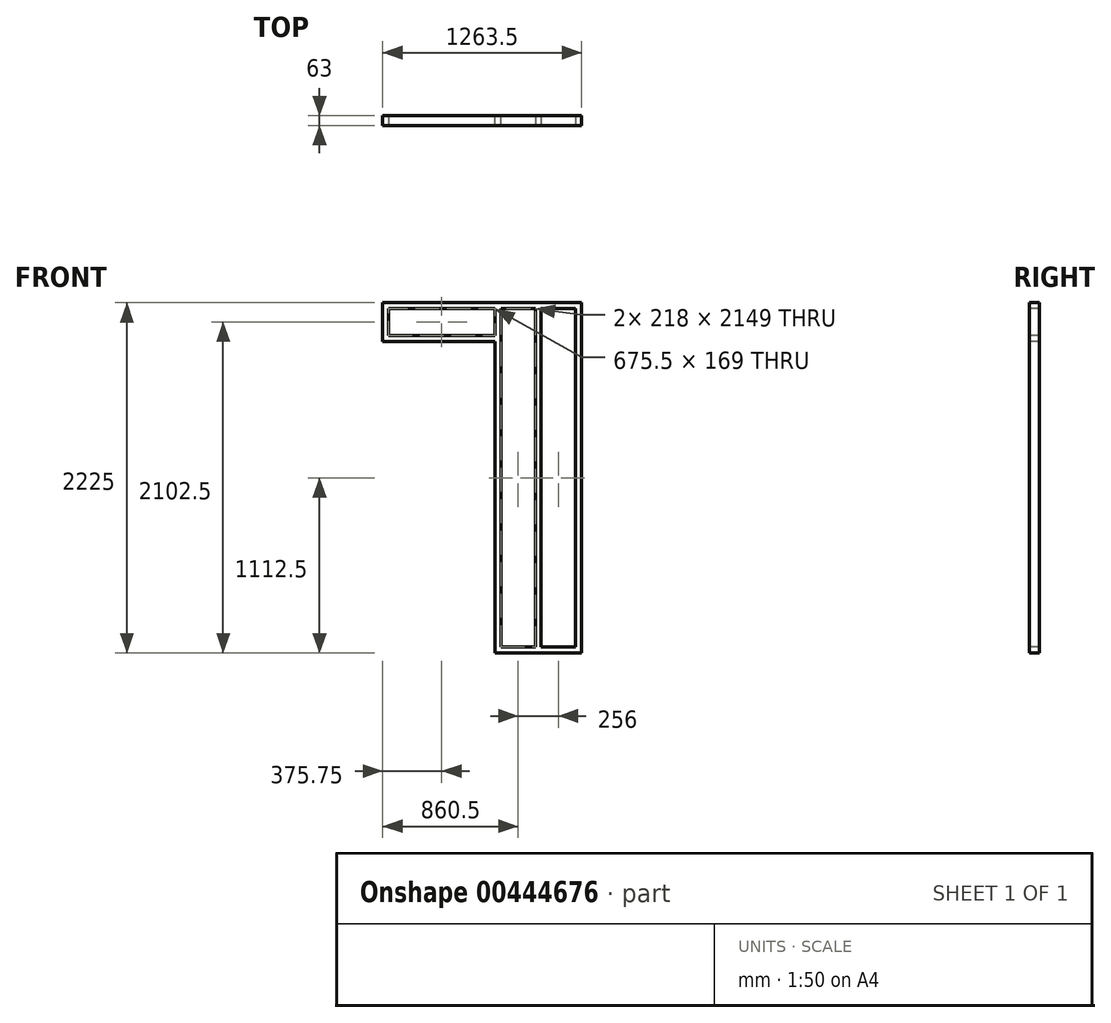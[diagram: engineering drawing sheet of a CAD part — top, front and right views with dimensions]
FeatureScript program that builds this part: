
annotation { "Feature Type Name" : "Feature", "Feature Type Description" : "" }
export const myFeature = defineFeature(function(context is Context, id is Id, definition is map)
    precondition{}
    {
        {
            var Q0;
            Q0=qCreatedBy(makeId("Top.planeOp"),FACE);
            var sketch = newSketch(context, id + "F0", { "sketchPlane" : qUnion([Q0])});
            skLineSegment(sketch, "E0.bottom", {"start": v(0, 0) * mm, "end": v(-550, 0) * mm});
            skLineSegment(sketch, "E0.top", {"start": v(0, 63) * mm, "end": v(-550, 63) * mm});
            skLineSegment(sketch, "E0.left", {"start": v(0, 0) * mm, "end": v(0, 63) * mm});
            skLineSegment(sketch, "E0.right", {"start": v(-550, 0) * mm, "end": v(-550, 63) * mm});
            skSolve(sketch);
        }
        {
            var Q0;
            Q0 = qSketchRegion(id + "F0", true);
            extrude(context, id + "F1", {"entities" : qUnion([Q0]), "depth" : 38 * mm});
        }
        {
            var Q0;
            Q0=makeQuery(id+"F1.opExtrude","CAP_FACE",FACE,{"disambiguationData":[OSD([sQuery(id+"F0.wireOp",EDGE,"E0.bottom"),sQuery(id+"F0.wireOp",EDGE,"E0.top"),sQuery(id+"F0.wireOp",EDGE,"E0.left"),sQuery(id+"F0.wireOp",EDGE,"E0.right")])],"isStart":false});
            var sketch = newSketch(context, id + "F2", { "sketchPlane" : qUnion([Q0])});
            skLineSegment(sketch, "E1.bottom", {"start": v(-550, 0) * mm, "end": v(-512, 0) * mm});
            skLineSegment(sketch, "E1.top", {"start": v(-550, 63) * mm, "end": v(-512, 63) * mm});
            skLineSegment(sketch, "E1.left", {"start": v(-550, 0) * mm, "end": v(-550, 63) * mm});
            skLineSegment(sketch, "E1.right", {"start": v(-512, 0) * mm, "end": v(-512, 63) * mm});
            skSolve(sketch);
        }
        {
            var Q0;
            Q0 = qSketchRegion(id + "F2", true);
            extrude(context, id + "F3", {"entities" : qUnion([Q0]), "operationType" : NewBodyOperationType.ADD, "depth" : 2149 * mm});
        }
        {
            var Q0;
            Q0=makeQuery(id+"F1.opExtrude","CAP_FACE",FACE,{"disambiguationData":[OSD([sQuery(id+"F0.wireOp",EDGE,"E0.bottom"),sQuery(id+"F0.wireOp",EDGE,"E0.top"),sQuery(id+"F0.wireOp",EDGE,"E0.left"),sQuery(id+"F0.wireOp",EDGE,"E0.right")])],"isStart":false});
            var sketch = newSketch(context, id + "F4", { "sketchPlane" : qUnion([Q0])});
            skLineSegment(sketch, "E2.bottom", {"start": v(0, 63) * mm, "end": v(-38, 63) * mm});
            skLineSegment(sketch, "E2.top", {"start": v(0, 0) * mm, "end": v(-38, 0) * mm});
            skLineSegment(sketch, "E2.left", {"start": v(0, 63) * mm, "end": v(0, 0) * mm});
            skLineSegment(sketch, "E2.right", {"start": v(-38, 63) * mm, "end": v(-38, 0) * mm});
            skSolve(sketch);
        }
        {
            var Q0;
            Q0 = qSketchRegion(id + "F4", true);
            extrude(context, id + "F5", {"entities" : qUnion([Q0]), "operationType" : NewBodyOperationType.ADD, "depth" : 2149 * mm});
        }
        {
            var Q0;
            Q0=makeQuery(id+"F1.opExtrude","CAP_FACE",FACE,{"disambiguationData":[OSD([sQuery(id+"F0.wireOp",EDGE,"E0.bottom"),sQuery(id+"F0.wireOp",EDGE,"E0.top"),sQuery(id+"F0.wireOp",EDGE,"E0.left"),sQuery(id+"F0.wireOp",EDGE,"E0.right")])],"isStart":false});
            var sketch = newSketch(context, id + "F6", { "sketchPlane" : qUnion([Q0])});
            skLineSegment(sketch, "E3.bottom", {"start": v(-294, 63) * mm, "end": v(-256, 63) * mm});
            skLineSegment(sketch, "E3.top", {"start": v(-294, 0) * mm, "end": v(-256, 0) * mm});
            skLineSegment(sketch, "E3.left", {"start": v(-294, 63) * mm, "end": v(-294, 0) * mm});
            skLineSegment(sketch, "E3.right", {"start": v(-256, 63) * mm, "end": v(-256, 0) * mm});
            skSolve(sketch);
        }
        {
            var Q0;
            Q0 = qSketchRegion(id + "F6", true);
            extrude(context, id + "F7", {"entities" : qUnion([Q0]), "operationType" : NewBodyOperationType.ADD, "depth" : 2149 * mm});
        }
        {
            var Q0;
            Q0=makeQuery(id+"F5.opExtrude","CAP_FACE",FACE,{"disambiguationData":[OSD([sQuery(id+"F4.wireOp",EDGE,"E2.bottom"),sQuery(id+"F4.wireOp",EDGE,"E2.top"),sQuery(id+"F4.wireOp",EDGE,"E2.left"),sQuery(id+"F4.wireOp",EDGE,"E2.right")])],"isStart":false});
            var sketch = newSketch(context, id + "F8", { "sketchPlane" : qUnion([Q0])});
            skLineSegment(sketch, "E4.bottom", {"start": v(0, 0) * mm, "end": v(-1263.5, 0) * mm});
            skLineSegment(sketch, "E4.top", {"start": v(0, 63) * mm, "end": v(-1263.5, 63) * mm});
            skLineSegment(sketch, "E4.left", {"start": v(0, 0) * mm, "end": v(0, 63) * mm});
            skLineSegment(sketch, "E4.right", {"start": v(-1263.5, 0) * mm, "end": v(-1263.5, 63) * mm});
            skSolve(sketch);
        }
        {
            var Q0;
            Q0 = qSketchRegion(id + "F8", true);
            extrude(context, id + "F9", {"entities" : qUnion([Q0]), "operationType" : NewBodyOperationType.ADD, "depth" : 38 * mm});
        }
        {
            var Q0;
            Q0=makeQuery(id+"F3.boolean.opBoolean","MERGE",FACE,{"derivedFrom":[makeQuery(id+"F1.opExtrude","SWEPT_FACE",FACE,{"disambiguationData":[OSD([sQuery(id+"F0.wireOp",EDGE,"E0.right")])]}),makeQuery(id+"F3.opExtrude","SWEPT_FACE",FACE,{"disambiguationData":[OSD([sQuery(id+"F2.wireOp",EDGE,"E1.left")])]})]});
            var sketch = newSketch(context, id + "F10", { "sketchPlane" : qUnion([Q0])});
            skLineSegment(sketch, "E5.bottom", {"start": v(-63, 2018) * mm, "end": v(0, 2018) * mm});
            skLineSegment(sketch, "E5.top", {"start": v(-63, 1980) * mm, "end": v(0, 1980) * mm});
            skLineSegment(sketch, "E5.left", {"start": v(-63, 2018) * mm, "end": v(-63, 1980) * mm});
            skLineSegment(sketch, "E5.right", {"start": v(0, 2018) * mm, "end": v(0, 1980) * mm});
            skSolve(sketch);
        }
        {
            var Q0;
            Q0 = qSketchRegion(id + "F10", true);
            extrude(context, id + "F11", {"entities" : qUnion([Q0]), "operationType" : NewBodyOperationType.ADD, "depth" : 713.5 * mm});
        }
        {
            var Q0;
            Q0=makeQuery(id+"F11.opExtrude","SWEPT_FACE",FACE,{"disambiguationData":[OSD([sQuery(id+"F10.wireOp",EDGE,"E5.bottom")])]});
            var sketch = newSketch(context, id + "F12", { "sketchPlane" : qUnion([Q0])});
            skLineSegment(sketch, "E6.bottom", {"start": v(-1263.5, 63) * mm, "end": v(-1225.5, 63) * mm});
            skLineSegment(sketch, "E6.top", {"start": v(-1263.5, 0) * mm, "end": v(-1225.5, 0) * mm});
            skLineSegment(sketch, "E6.left", {"start": v(-1263.5, 63) * mm, "end": v(-1263.5, 0) * mm});
            skLineSegment(sketch, "E6.right", {"start": v(-1225.5, 63) * mm, "end": v(-1225.5, 0) * mm});
            skSolve(sketch);
        }
        {
            var Q0;
            Q0 = qSketchRegion(id + "F12", true);
            extrude(context, id + "F13", {"entities" : qUnion([Q0]), "operationType" : NewBodyOperationType.ADD, "depth" : 169 * mm});
        }
    });
